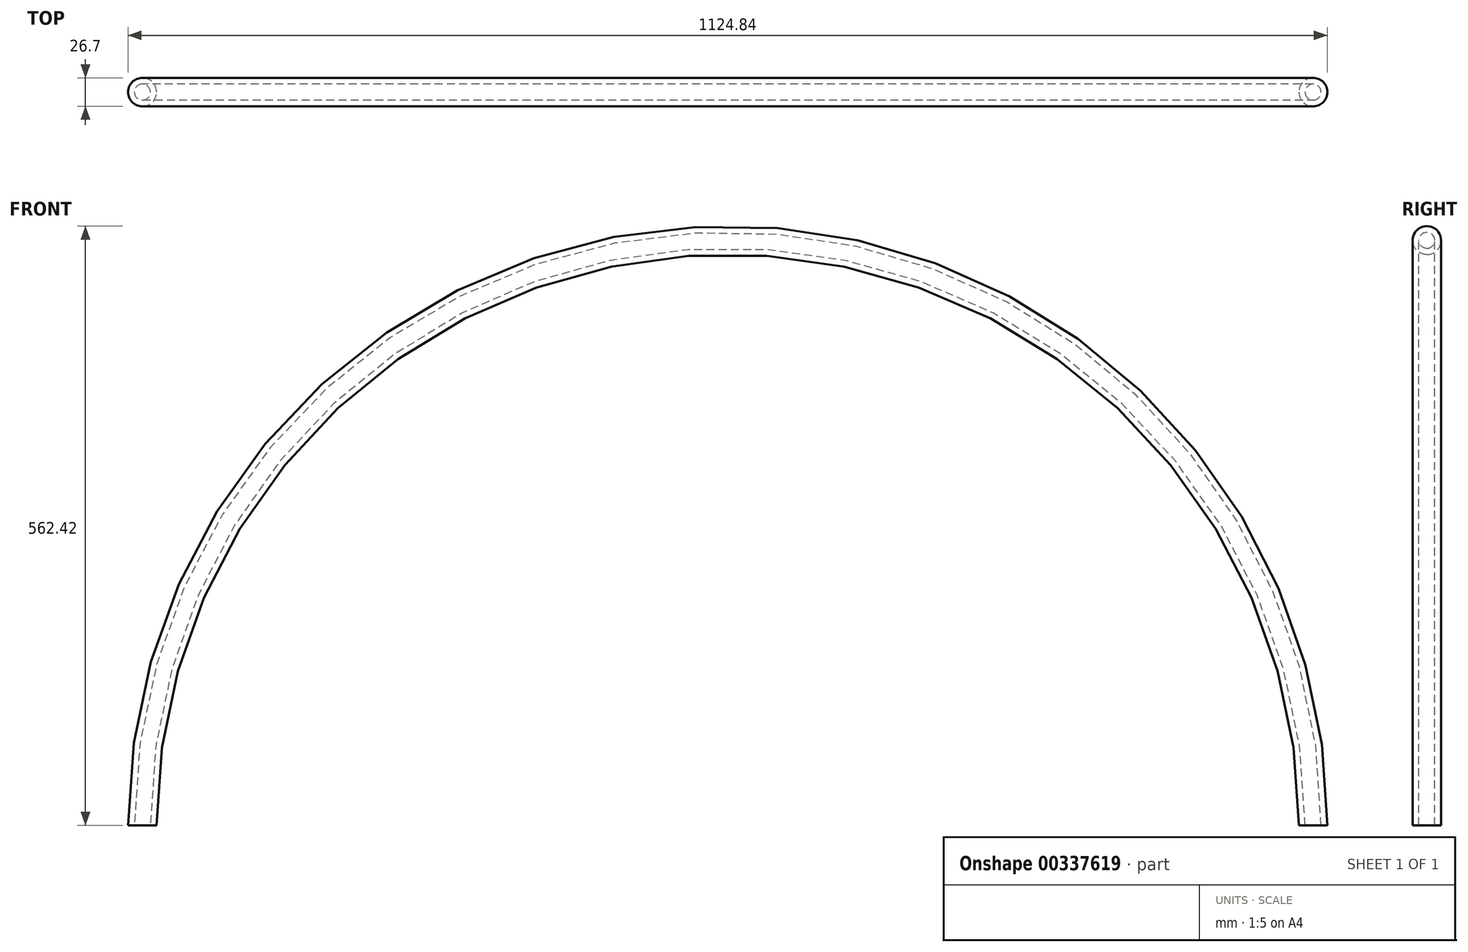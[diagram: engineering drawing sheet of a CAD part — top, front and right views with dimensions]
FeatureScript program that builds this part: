
annotation { "Feature Type Name" : "Feature", "Feature Type Description" : "" }
export const myFeature = defineFeature(function(context is Context, id is Id, definition is map)
    precondition{}
    {
        {
            var Q0;
            Q0=qCreatedBy(makeId("Top.planeOp"),FACE);
            var sketch = newSketch(context, id + "F0", { "sketchPlane" : qUnion([Q0])});
            skCircle(sketch, "E0", {"center": v(-49.07, 0) * mm, "radius": 13.35 * mm});
            skCircle(sketch, "E1", {"center": v(-49.07, 0) * mm, "radius": 7.5 * mm});
            skLineSegment(sketch, "E2", {"start": v(0, 0) * mm, "end": v(0, 41.06) * mm, "construction": true});
            skLineSegment(sketch, "E3", {"start": v(500, 41.06) * mm, "end": v(500, -28.82) * mm, "construction": true});
            skSolve(sketch);
        }
        {
            var Q0;
            Q0=makeQuery(id+"F0.imprint","IMPRINT",FACE,{"disambiguationData":[TD([[makeQuery(id+"F0.imprint","IMPRINT",EDGE,{"derivedFrom":sQuery(id+"F0.wireOp",EDGE,"E0")}),1.0]])]});
            var Q1;
            Q1=sQuery(id+"F0.wireOp",EDGE,"E3");
            revolve(context, id + "F1", {"entities" : qUnion([Q0]), "axis" : qUnion([Q1]), "revolveType" : RevolveType.ONE_DIRECTION, "oppositeDirection" : true, "angle" : 180 * degree});
        }
    });
